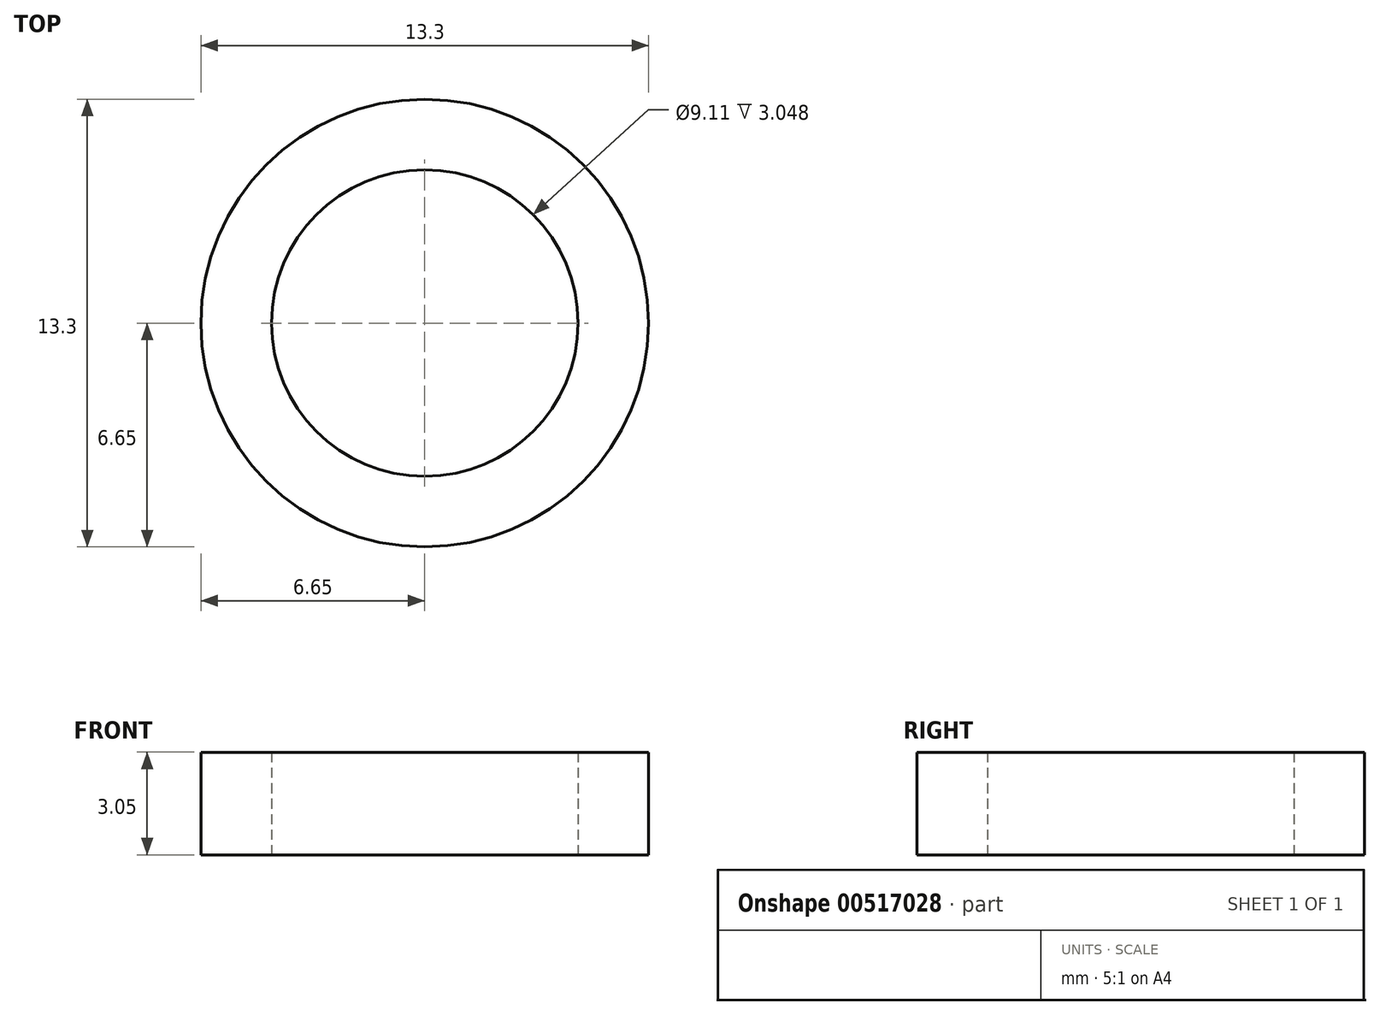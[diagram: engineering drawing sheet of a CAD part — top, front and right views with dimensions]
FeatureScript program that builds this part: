
annotation { "Feature Type Name" : "Feature", "Feature Type Description" : "" }
export const myFeature = defineFeature(function(context is Context, id is Id, definition is map)
    precondition{}
    {
        {
            var Q0;
            Q0=qCreatedBy(makeId("Top.planeOp"),FACE);
            var sketch = newSketch(context, id + "F0", { "sketchPlane" : qUnion([Q0])});
            skCircle(sketch, "E0", {"center": v(0, 0) * mm, "radius": 4.55 * mm});
            skCircle(sketch, "E1", {"center": v(0, 0) * mm, "radius": 6.65 * mm});
            skSolve(sketch);
        }
        {
            var Q0;
            Q0=makeQuery(id+"F0.imprint","IMPRINT",FACE,{"disambiguationData":[TD([[makeQuery(id+"F0.imprint","IMPRINT",EDGE,{"derivedFrom":sQuery(id+"F0.wireOp",EDGE,"E0")}),-1.0]])]});
            extrude(context, id + "F1", {"entities" : qUnion([Q0]), "depth" : 3.05 * mm, "offsetDistance" : 25.4 * mm});
        }
    });
